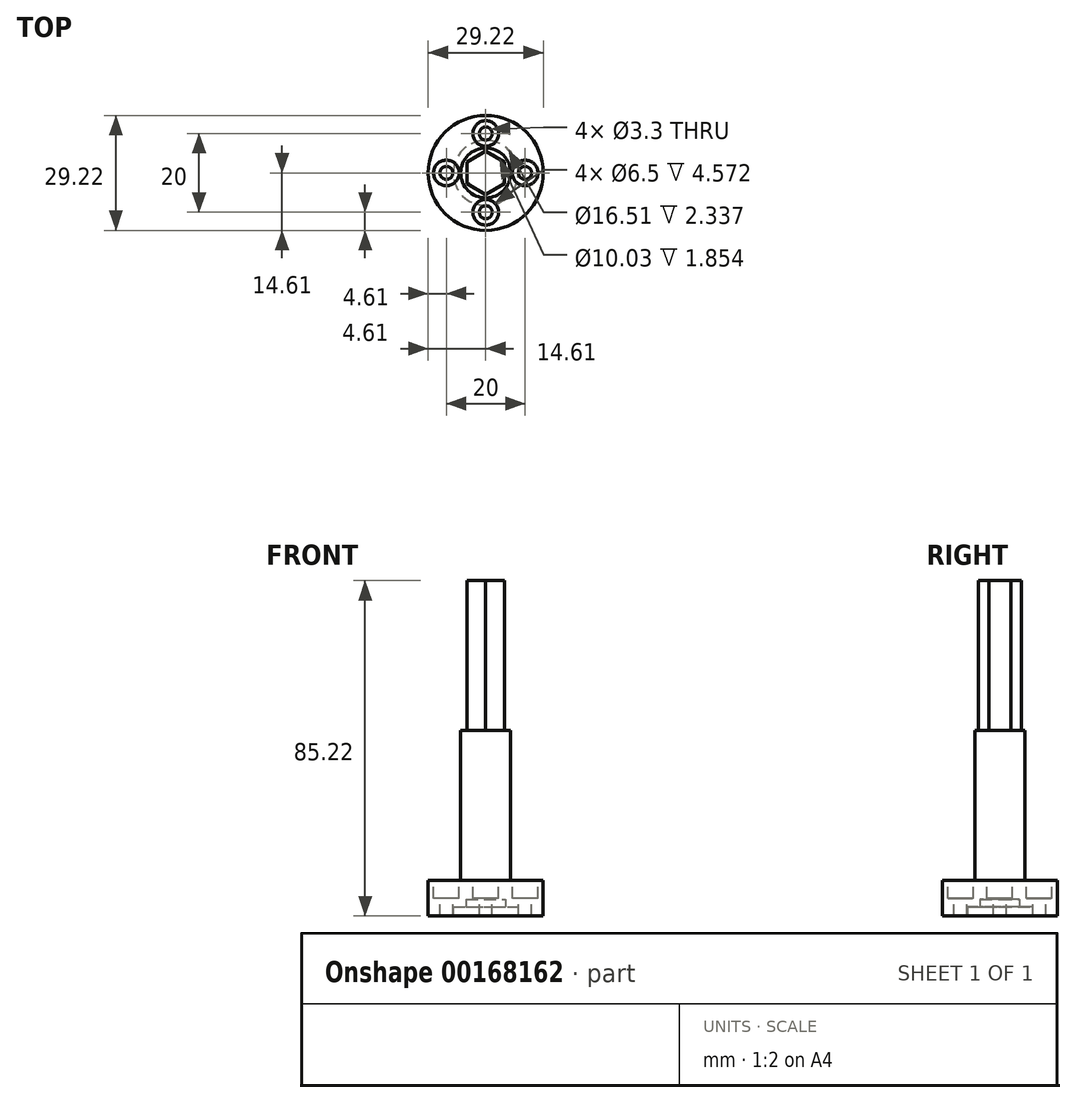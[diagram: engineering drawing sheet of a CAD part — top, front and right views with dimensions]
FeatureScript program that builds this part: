
annotation { "Feature Type Name" : "Feature", "Feature Type Description" : "" }
export const myFeature = defineFeature(function(context is Context, id is Id, definition is map)
    precondition{}
    {
        {
            var Q0;
            Q0=qCreatedBy(makeId("Top.planeOp"),FACE);
            var sketch = newSketch(context, id + "F0", { "sketchPlane" : qUnion([Q0])});
            skCircle(sketch, "E0", {"center": v(0, 0) * mm, "radius": 14.6 * mm});
            skSolve(sketch);
        }
        {
            var Q0;
            Q0=makeQuery(id+"F0.imprint","IMPRINT",FACE,{"disambiguationData":[TD([[makeQuery(id+"F0.imprint","IMPRINT",EDGE,{"derivedFrom":sQuery(id+"F0.wireOp",EDGE,"E0")}),1.0]])]});
            extrude(context, id + "F1", {"entities" : qUnion([Q0]), "depth" : 9.02 * mm});
        }
        {
            var Q0;
            Q0=makeQuery(id+"F1.opExtrude","CAP_FACE",FACE,{"disambiguationData":[OSD([sQuery(id+"F0.wireOp",EDGE,"E0")])],"isStart":false});
            var sketch = newSketch(context, id + "F2", { "sketchPlane" : qUnion([Q0])});
            skCircle(sketch, "E1", {"center": v(0, 0) * mm, "radius": 6.35 * mm});
            skSolve(sketch);
        }
        {
            var Q0;
            Q0=qSketchRegion(id+"F2",true);
            extrude(context, id + "F3", {"entities" : qUnion([Q0]), "operationType" : NewBodyOperationType.ADD, "depth" : 38.1 * mm});
        }
        {
            var Q0;
            Q0=makeQuery(id+"F3.opExtrude","CAP_FACE",FACE,{"disambiguationData":[OSD([sQuery(id+"F2.wireOp",EDGE,"E1")])],"isStart":false});
            var sketch = newSketch(context, id + "F4", { "sketchPlane" : qUnion([Q0])});
            skCircle(sketch, "E2.cCircle", {"center": v(0, 0) * mm, "radius": 4.76 * mm, "construction": true});
            skLineSegment(sketch, "E2.0", {"start": v(4.76, 2.75) * mm, "end": v(4.76, -2.75) * mm});
            skLineSegment(sketch, "E2.1", {"start": v(4.76, -2.75) * mm, "end": v(0, -5.5) * mm});
            skLineSegment(sketch, "E2.2", {"start": v(0, -5.5) * mm, "end": v(-4.76, -2.75) * mm});
            skLineSegment(sketch, "E2.3", {"start": v(-4.76, -2.75) * mm, "end": v(-4.76, 2.75) * mm});
            skLineSegment(sketch, "E2.4", {"start": v(-4.76, 2.75) * mm, "end": v(0, 5.5) * mm});
            skLineSegment(sketch, "E2.5", {"start": v(0, 5.5) * mm, "end": v(4.76, 2.75) * mm});
            skPoint(sketch, "E2.0.midPoint", {"position": v(4.76, 0) * mm});
            skSolve(sketch);
        }
        {
            var Q0;
            Q0=makeQuery(id+"F4.imprint","IMPRINT",FACE,{"disambiguationData":[TD([[makeQuery(id+"F4.imprint","IMPRINT",EDGE,{"derivedFrom":sQuery(id+"F4.wireOp",EDGE,"E2.0")}),-1.0]])]});
            extrude(context, id + "F5", {"entities" : qUnion([Q0]), "operationType" : NewBodyOperationType.ADD, "depth" : 38.1 * mm});
        }
        {
            var Q0;
            Q0=makeQuery(id+"F1.opExtrude","CAP_FACE",FACE,{"disambiguationData":[OSD([sQuery(id+"F0.wireOp",EDGE,"E0")])],"isStart":true});
            var sketch = newSketch(context, id + "F6", { "sketchPlane" : qUnion([Q0])});
            skCircle(sketch, "E3", {"center": v(0, 0) * mm, "radius": 8.26 * mm});
            skSolve(sketch);
        }
        {
            var Q0;
            Q0=qSketchRegion(id+"F6",true);
            extrude(context, id + "F7", {"entities" : qUnion([Q0]), "operationType" : NewBodyOperationType.REMOVE, "oppositeDirection" : true, "depth" : 2.34 * mm});
        }
        {
            var Q0;
            Q0=makeQuery(id+"F1.opExtrude","CAP_FACE",FACE,{"disambiguationData":[OSD([sQuery(id+"F0.wireOp",EDGE,"E0")])],"isStart":true});
            var sketch = newSketch(context, id + "F8", { "sketchPlane" : qUnion([Q0])});
            skCircle(sketch, "E4", {"center": v(0, 0) * mm, "radius": 5.02 * mm});
            skSolve(sketch);
        }
        {
            var Q0;
            Q0=qSketchRegion(id+"F8",true);
            extrude(context, id + "F9", {"entities" : qUnion([Q0]), "operationType" : NewBodyOperationType.REMOVE, "oppositeDirection" : true, "depth" : 4.2 * mm});
        }
        {
            var Q0;
            Q0=makeQuery(id+"F1.opExtrude","CAP_FACE",FACE,{"disambiguationData":[OSD([sQuery(id+"F0.wireOp",EDGE,"E0")])],"isStart":false});
            var sketch = newSketch(context, id + "F10", { "sketchPlane" : qUnion([Q0])});
            skPoint(sketch, "E5", {"position": v(-10, 0) * mm});
            skPoint(sketch, "E6", {"position": v(0, 10) * mm});
            skPoint(sketch, "E7", {"position": v(10, 0) * mm});
            skPoint(sketch, "E8", {"position": v(0, -10) * mm});
            skCircle(sketch, "E9", {"center": v(0, 0) * mm, "radius": 10 * mm, "construction": true});
            skSolve(sketch);
        }
        {
            var Q0;
            Q0=sQuery(id+"F10.wireOp",VERTEX,"E8");
            var Q1;
            Q1=sQuery(id+"F10.wireOp",VERTEX,"E5");
            var Q2;
            Q2=sQuery(id+"F10.wireOp",VERTEX,"E6");
            var Q3;
            Q3=sQuery(id+"F10.wireOp",VERTEX,"E7");
            var Q4;
            Q4=makeQuery(id+"F1.opExtrude","SWEPT_BODY",BODY,{"disambiguationData":[OSD([sQuery(id+"F0.wireOp",EDGE,"E0")])]});
            hole(context, id + "F11", {"style" : HoleStyle.C_BORE, "endStyle" : HoleEndStyle.THROUGH, "standardTappedOrClearance" : lookupTablePath({ "standard" : "ISO", "fit" : "Normal", "size" : "M3", "type" : "Clearance" }), "standardBlindInLast" : lookupTablePath({ "fit" : "Standard", "standard" : "ISO", "size" : "M3", "type" : "Clearance" }), "holeDiameter" : 3.3 * mm, "cBoreDiameter" : 6.5 * mm, "cBoreDepth" : 4.57 * mm, "locations" : qUnion([Q0, Q1, Q2, Q3]), "scope" : qUnion([Q4]), "isTappedThrough" : true});
        }
    });
